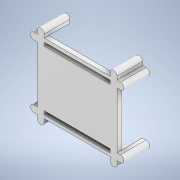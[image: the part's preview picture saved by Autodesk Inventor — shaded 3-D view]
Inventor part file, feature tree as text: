
AUTODESK INVENTOR PART (.ipt)
format: ipt  version: 2020 (Build 240168000, 168)  size: 245,248 bytes
history: native  units: in
note: dims shown in document units (in); Inventor stores cm internally (conversion verified against a paired STEP export)
features: other x3, extrude x2, sketch x2, plane x1
ambient origin geometry x8: Origin, YZ Plane, XZ Plane, XY Plane, X Axis, Y Axis, Z Axis, Center Point
bodies: Solid1 (feature_tree)
feature tree (8):
  plane  "Work Plane1"
  extrude  "Extrusion2"  Depth=0.1in TaperAngle=0.0deg
  extrude  "Extrusion3"  [1 undecoded]
  sketch  "Sketch2"  dims[d21=0.15in d22=0.15in d23=0.15in d24=0.15in d25=0.15in d26=0.15in d27=0.15in d28=0.15in d29=0.15in d30=0.15in d31=0.15in d32=0.15in d33=0.15in d34=0.15in d35=0.15in d36=0.15in d37=0.075in d38=0.075in d39=0.075in d40=0.1in d41=0.0in]
  sketch  "Sketch4"  dims[d42=0.4545in d43=0.0in]
  other  "<userpath>\Documents\Inventor\Drone\Assembly.iam"
  other  "Assembly.iam"
  other  "Pixfalcon-Flight-Controller v1:1"
note: 1 required parameter value undecoded (feature->parameter linkage not recoverable at this tier; creation-order binding heuristic only, values carry confidence <= 0.55)
